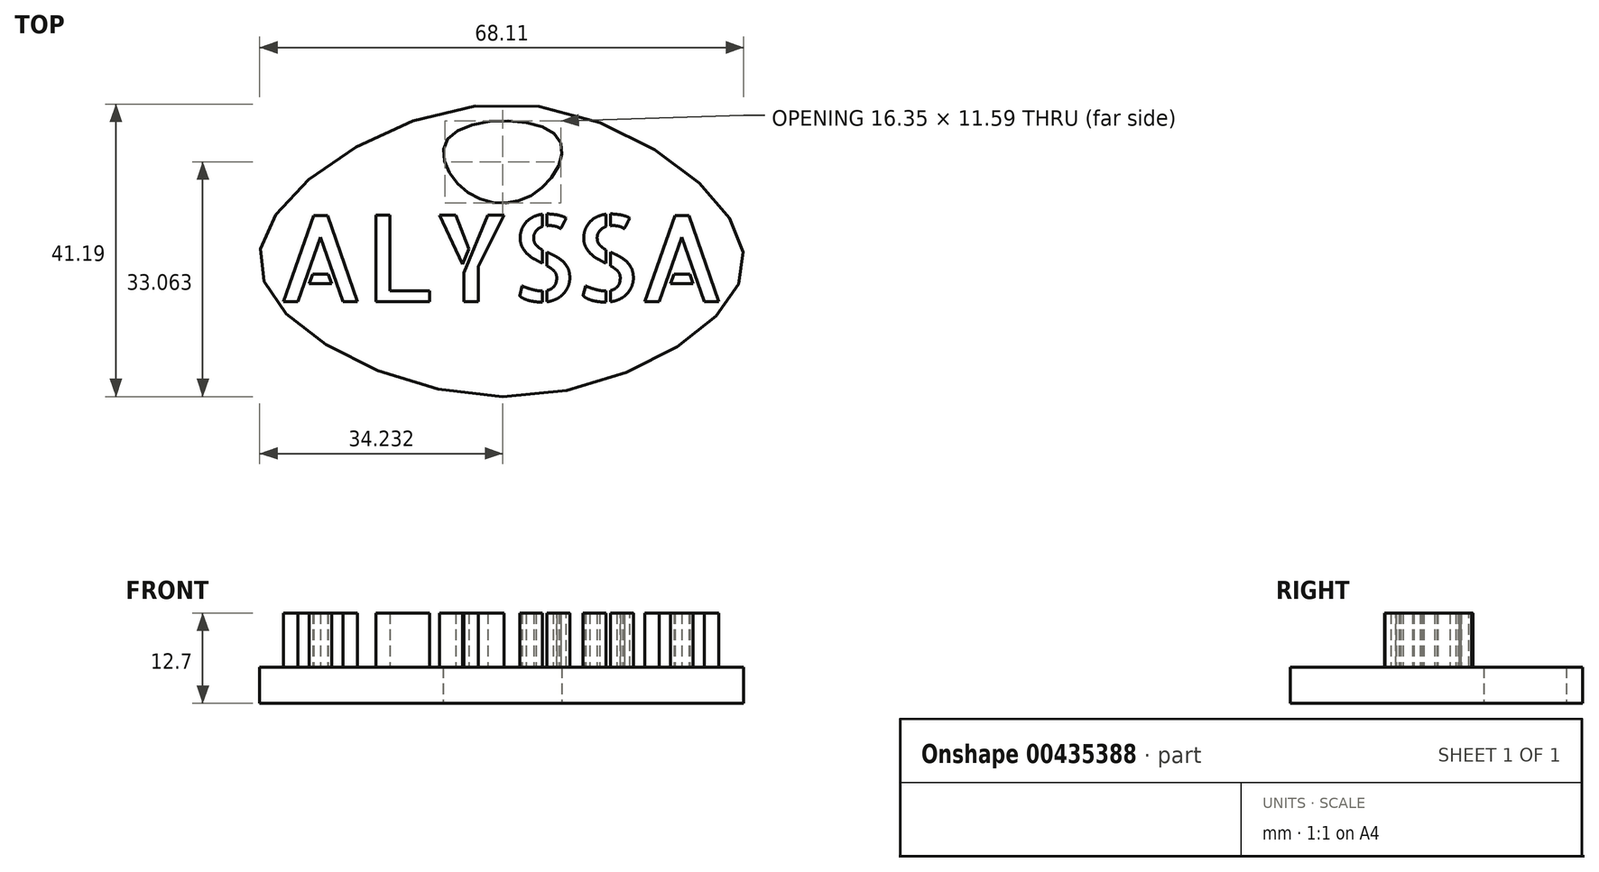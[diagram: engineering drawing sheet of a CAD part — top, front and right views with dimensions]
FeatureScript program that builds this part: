
annotation { "Feature Type Name" : "Feature", "Feature Type Description" : "" }
export const myFeature = defineFeature(function(context is Context, id is Id, definition is map)
    precondition{}
    {
        {
            var Q0;
            Q0=qCreatedBy(makeId("Top.planeOp"),FACE);
            var sketch = newSketch(context, id + "F0", { "sketchPlane" : qUnion([Q0])});
            skText(sketch, "E0", { "text": "ALYSSA", "fontName": "AllertaStencil-Regular.ttf"});
            const initialGuessF0  = {"E0": [0, 0, 1, 0, 0.01217]};
            skSetInitialGuess(sketch, initialGuessF0);
            skSolve(sketch);
        }
        {
            var Q0;
            Q0=makeQuery(id+"F0.imprint","IMPRINT",FACE,{"disambiguationData":[TD([[makeQuery(id+"F0.imprint","IMPRINT",EDGE,{"derivedFrom":sQuery(id+"F0.wireOp",EDGE,"E0.sketch_text.stroke-134")}),-1.0]])]});
            var sketch = newSketch(context, id + "F1", { "sketchPlane" : qUnion([Q0])});
            skFitSpline(sketch, "E1", {"points": [v(0, 12.24) * mm, v(32.83, 27.8) * mm, v(63.71, 12) * mm, v(63.71, 0) * mm, v(32.83, -13.38) * mm, v(0, 0) * mm, v(0, 12.24) * mm]});
            skSolve(sketch);
        }
        {
            var Q0;
            Q0=makeQuery(id+"F1.imprint","IMPRINT",FACE,{"disambiguationData":[TD([[makeQuery(id+"F1.imprint","IMPRINT",EDGE,{"derivedFrom":sQuery(id+"F1.wireOp",EDGE,"E1")}),-1.0]])]});
            extrude(context, id + "F2", {"entities" : qUnion([Q0]), "depth" : 5.08 * mm});
        }
        {
            var Q0;
            Q0 = qSketchRegion(id + "F0", true);
            extrude(context, id + "F3", {"entities" : qUnion([Q0]), "operationType" : NewBodyOperationType.ADD, "depth" : 12.7 * mm});
        }
        {
            var Q0;
            Q0=qCreatedBy(makeId("Top.planeOp"),FACE);
            var sketch = newSketch(context, id + "F4", { "sketchPlane" : qUnion([Q0])});
            skCircle(sketch, "E2", {"center": v(30.98, 20.45) * mm, "radius": 5.53 * mm});
            skSolve(sketch);
        }
        {
            var Q0;
            Q0 = qSketchRegion(id + "F4", true);
            extrude(context, id + "F5", {"entities" : qUnion([Q0]), "operationType" : NewBodyOperationType.REMOVE, "endBound" : BoundingType.THROUGH_ALL, "oppositeDirection" : true, "depth" : 25.4 * mm});
        }
        {
            var Q0;
            Q0=makeQuery(id+"F2.opExtrude","CAP_FACE",FACE,{"disambiguationData":[OSD([sQuery(id+"F0.wireOp",EDGE,"E0.sketch_text.stroke-134"),sQuery(id+"F0.wireOp",EDGE,"E0.sketch_text.stroke-135"),sQuery(id+"F0.wireOp",EDGE,"E0.sketch_text.stroke-136"),sQuery(id+"F0.wireOp",EDGE,"E0.sketch_text.stroke-137"),sQuery(id+"F1.wireOp",EDGE,"E1")])],"isStart":false});
            var sketch = newSketch(context, id + "F6", { "sketchPlane" : qUnion([Q0])});
            skFitSpline(sketch, "E3", {"points": [v(27.07, 15.34) * mm, v(37, 15.64) * mm, v(39.4, 23.46) * mm, v(24.36, 23.16) * mm, v(27.07, 15.34) * mm]});
            skSolve(sketch);
        }
        {
            var Q0;
            Q0=makeQuery(id+"F6.imprint","IMPRINT",FACE,{"disambiguationData":[TD([[makeQuery(id+"F6.imprint","IMPRINT",EDGE,{"derivedFrom":sQuery(id+"F6.wireOp",EDGE,"E3")}),1.0]])]});
            var Q1;
            Q1=sQuery(id+"F6.wireOp",EDGE,"E3");
            extrude(context, id + "F7", {"entities" : qUnion([Q0]), "operationType" : NewBodyOperationType.REMOVE, "surfaceEntities" : qUnion([Q1]), "endBound" : BoundingType.THROUGH_ALL, "oppositeDirection" : true, "depth" : 25.4 * mm});
        }
    });
